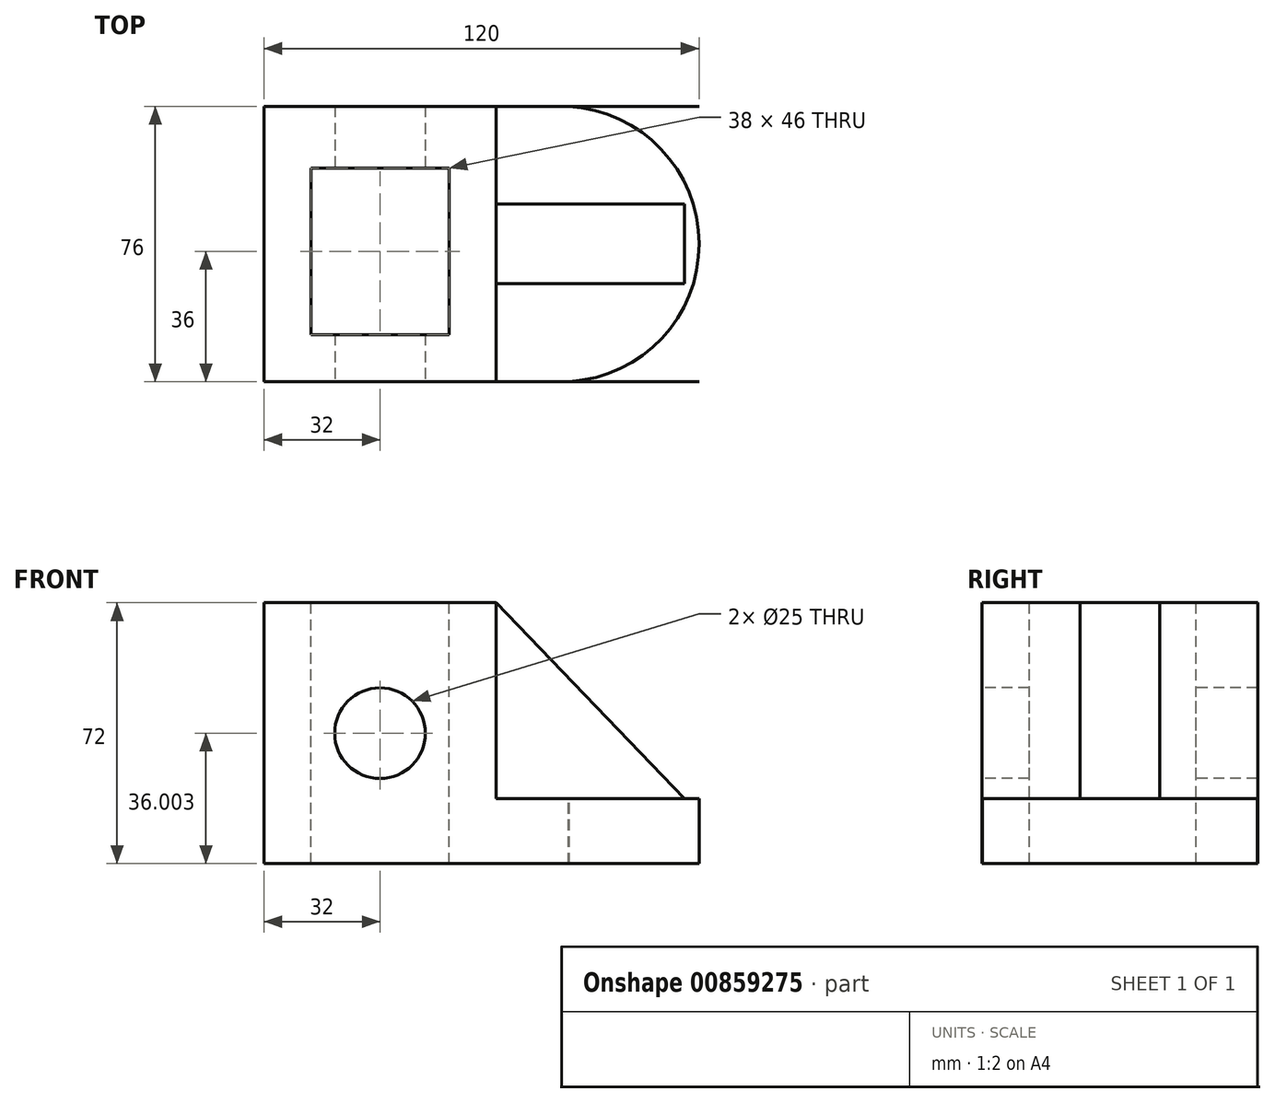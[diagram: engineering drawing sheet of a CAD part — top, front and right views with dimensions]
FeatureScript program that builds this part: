
annotation { "Feature Type Name" : "Feature", "Feature Type Description" : "" }
export const myFeature = defineFeature(function(context is Context, id is Id, definition is map)
    precondition{}
    {
        {
            var Q0;
            Q0=qCreatedBy(makeId("Front.planeOp"),FACE);
            var sketch = newSketch(context, id + "F0", { "sketchPlane" : qUnion([Q0])});
            skLineSegment(sketch, "E0", {"start": v(0, -11) * mm, "end": v(-120, -11) * mm});
            skLineSegment(sketch, "E1", {"start": v(-120, -11) * mm, "end": v(-120, 61) * mm});
            skLineSegment(sketch, "E2", {"start": v(-120, 61) * mm, "end": v(-56, 61) * mm});
            skLineSegment(sketch, "E3", {"start": v(-56, 61) * mm, "end": v(-56, 7) * mm});
            skLineSegment(sketch, "E4", {"start": v(-56, 7) * mm, "end": v(0, 7) * mm});
            skLineSegment(sketch, "E5", {"start": v(0, 7) * mm, "end": v(0, -11) * mm});
            skCircle(sketch, "E6", {"center": v(-88, 25) * mm, "radius": 12.5 * mm});
            skPoint(sketch, "E6.centerSnap0", {"position": v(-120, 25) * mm});
            skPoint(sketch, "E6.centerSnap1", {"position": v(-88, 61) * mm});
            skSolve(sketch);
        }
        {
            var Q0;
            Q0=makeQuery(id+"F0.imprint","IMPRINT",FACE,{"disambiguationData":[TD([[makeQuery(id+"F0.imprint","IMPRINT",EDGE,{"derivedFrom":sQuery(id+"F0.wireOp",EDGE,"E0")}),-1.0]])]});
            extrude(context, id + "F1", {"entities" : qUnion([Q0]), "oppositeDirection" : true, "depth" : 76 * mm, "offsetDistance" : 25 * mm});
        }
        {
            var Q0;
            Q0=makeQuery(id+"F1.opExtrude","SWEPT_FACE",FACE,{"disambiguationData":[OSD([sQuery(id+"F0.wireOp",EDGE,"E2")])]});
            var sketch = newSketch(context, id + "F2", { "sketchPlane" : qUnion([Q0])});
            skLineSegment(sketch, "E7.bottom", {"start": v(-107, 59) * mm, "end": v(-69, 59) * mm});
            skLineSegment(sketch, "E7.top", {"start": v(-107, 13) * mm, "end": v(-69, 13) * mm});
            skLineSegment(sketch, "E7.left", {"start": v(-107, 59) * mm, "end": v(-107, 13) * mm});
            skLineSegment(sketch, "E7.right", {"start": v(-69, 59) * mm, "end": v(-69, 13) * mm});
            skSolve(sketch);
        }
        {
            var Q0;
            Q0=makeQuery(id+"F2.imprint","IMPRINT",FACE,{"disambiguationData":[TD([[makeQuery(id+"F2.imprint","IMPRINT",EDGE,{"derivedFrom":sQuery(id+"F2.wireOp",EDGE,"E7.bottom")}),-1.0]])]});
            extrude(context, id + "F3", {"entities" : qUnion([Q0]), "operationType" : NewBodyOperationType.REMOVE, "oppositeDirection" : true, "depth" : 177 * mm, "offsetDistance" : 25 * mm});
        }
        {
            var Q0;
            Q0=makeQuery(id+"F1.opExtrude","SWEPT_FACE",FACE,{"disambiguationData":[OSD([sQuery(id+"F0.wireOp",EDGE,"E4")])]});
            var sketch = newSketch(context, id + "F4", { "sketchPlane" : qUnion([Q0])});
            skArc(sketch, "E8", {"start": v(-35.8, 0.06) * mm, "mid": v(0, 38.11) * mm, "end": v(-36.02, 75.95) * mm});
            skLineSegment(sketch, "E9", {"start": v(-36.02, 75.95) * mm, "end": v(0, 76) * mm});
            skLineSegment(sketch, "E10", {"start": v(0, 76) * mm, "end": v(0, 38) * mm});
            skLineSegment(sketch, "E11", {"start": v(0, 38) * mm, "end": v(0, 0) * mm});
            skLineSegment(sketch, "E12", {"start": v(0, 0) * mm, "end": v(-35.8, 0.06) * mm});
            skSolve(sketch);
        }
        {
            var Q0;
            {var subQ0=sQuery(id+"F4.wireOp",EDGE,"E9");Q0=makeQuery(id+"F4.imprint","IMPRINT",FACE,{"disambiguationData":[TD([[makeQuery(id+"F4.imprint","IMPRINT",EDGE,{"derivedFrom":subQ0}),-1.0]])]});}
            extrude(context, id + "F5", {"entities" : qUnion([Q0]), "operationType" : NewBodyOperationType.REMOVE, "oppositeDirection" : true, "depth" : 67 * mm, "offsetDistance" : 25 * mm});
        }
        {
            var Q0;
            Q0 = qSketchRegion(id + "F4", true);
            extrude(context, id + "F6", {"entities" : qUnion([Q0]), "operationType" : NewBodyOperationType.REMOVE, "oppositeDirection" : true, "depth" : 65 * mm, "offsetDistance" : 25 * mm});
        }
        {
            var Q0;
            Q0=makeQuery(id+"F1.opExtrude","SWEPT_FACE",FACE,{"disambiguationData":[OSD([sQuery(id+"F0.wireOp",EDGE,"E4")])]});
            var sketch = newSketch(context, id + "F7", { "sketchPlane" : qUnion([Q0])});
            skLineSegment(sketch, "E13", {"start": v(0, 38) * mm, "end": v(-4, 38) * mm});
            skLineSegment(sketch, "E14", {"start": v(-4, 49) * mm, "end": v(-4, 38) * mm});
            skLineSegment(sketch, "E15", {"start": v(-4, 38) * mm, "end": v(-4, 27) * mm});
            skLineSegment(sketch, "E16", {"start": v(-4, 27) * mm, "end": v(-56, 27) * mm});
            skLineSegment(sketch, "E17", {"start": v(-4, 49) * mm, "end": v(-56, 49) * mm});
            skLineSegment(sketch, "E18", {"start": v(-4, 38) * mm, "end": v(-56, 38) * mm});
            skPoint(sketch, "E18.endSnap0", {"position": v(-56, 38) * mm});
            skSolve(sketch);
        }
        {
            var Q0;
            Q0=makeQuery(id+"F7.imprint","IMPRINT",FACE,{"disambiguationData":[TD([[makeQuery(id+"F7.imprint","IMPRINT",EDGE,{"derivedFrom":sQuery(id+"F7.wireOp",EDGE,"E15")}),-1.0]])]});
            var Q1;
            Q1=makeQuery(id+"F7.imprint","IMPRINT",FACE,{"disambiguationData":[TD([[makeQuery(id+"F7.imprint","IMPRINT",EDGE,{"derivedFrom":sQuery(id+"F7.wireOp",EDGE,"E14")}),-1.0]])]});
            extrude(context, id + "F8", {"entities" : qUnion([Q0, Q1]), "operationType" : NewBodyOperationType.ADD, "depth" : 54 * mm, "offsetDistance" : 25 * mm});
        }
        {
            var Q0;
            Q0=makeQuery(id+"F8.opExtrude","SWEPT_FACE",FACE,{"disambiguationData":[OSD([sQuery(id+"F7.wireOp",EDGE,"E16")])]});
            var sketch = newSketch(context, id + "F9", { "sketchPlane" : qUnion([Q0])});
            skLineSegment(sketch, "E19", {"start": v(-4, 7) * mm, "end": v(-56, 61) * mm});
            skLineSegment(sketch, "E20", {"start": v(-56, 61) * mm, "end": v(-4, 61) * mm});
            skLineSegment(sketch, "E21", {"start": v(-4, 61) * mm, "end": v(-4, 7) * mm});
            skSolve(sketch);
        }
        {
            var Q0;
            Q0=makeQuery(id+"F9.imprint","IMPRINT",FACE,{"disambiguationData":[TD([[makeQuery(id+"F9.imprint","IMPRINT",EDGE,{"derivedFrom":sQuery(id+"F9.wireOp",EDGE,"E19")}),-1.0]])]});
            extrude(context, id + "F10", {"entities" : qUnion([Q0]), "operationType" : NewBodyOperationType.REMOVE, "oppositeDirection" : true, "depth" : 64 * mm, "offsetDistance" : 25 * mm});
        }
    });
